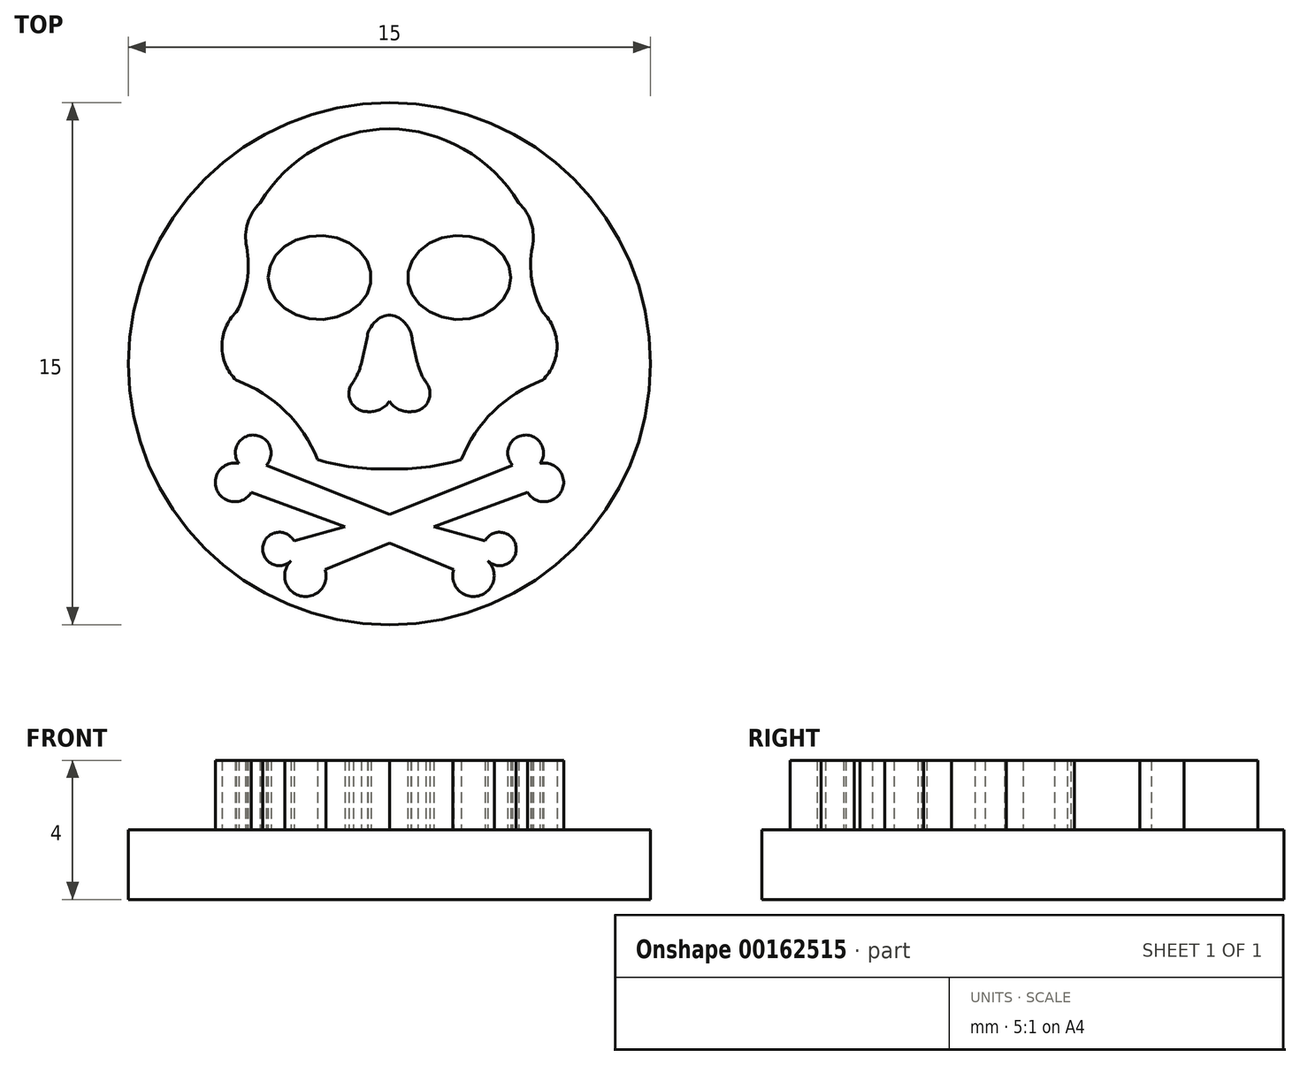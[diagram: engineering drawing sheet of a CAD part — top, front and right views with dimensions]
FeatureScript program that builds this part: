
annotation { "Feature Type Name" : "Feature", "Feature Type Description" : "" }
export const myFeature = defineFeature(function(context is Context, id is Id, definition is map)
    precondition{}
    {
        {
            var Q0;
            Q0=qCreatedBy(makeId("Top.planeOp"),FACE);
            var sketch = newSketch(context, id + "F0", { "sketchPlane" : qUnion([Q0])});
            skCircle(sketch, "E0", {"center": v(0, 0) * mm, "radius": 7.5 * mm});
            skSolve(sketch);
        }
        {
            var Q0;
            Q0=makeQuery(id+"F0.imprint","IMPRINT",FACE,{"disambiguationData":[TD([[makeQuery(id+"F0.imprint","IMPRINT",EDGE,{"derivedFrom":sQuery(id+"F0.wireOp",EDGE,"E0")}),1.0]])]});
            extrude(context, id + "F1", {"entities" : qUnion([Q0]), "depth" : 2 * mm});
        }
        {
            var Q0;
            Q0=makeQuery(id+"F1.opExtrude","CAP_FACE",FACE,{"disambiguationData":[OSD([sQuery(id+"F0.wireOp",EDGE,"E0")])],"isStart":false});
            var sketch = newSketch(context, id + "F2", { "sketchPlane" : qUnion([Q0])});
            skLineSegment(sketch, "E1", {"start": v(0, 8.52) * mm, "end": v(0, -8.58) * mm, "construction": true});
            skArc(sketch, "E2", {"start": v(-3.71, 4.63) * mm, "mid": v(-4.07, 4.04) * mm, "end": v(-4.1, 3.36) * mm});
            skArc(sketch, "E3", {"start": v(-4.4, 1.48) * mm, "mid": v(-4.1, 2.4) * mm, "end": v(-4.1, 3.36) * mm});
            skArc(sketch, "E4", {"start": v(-4.4, 1.48) * mm, "mid": v(-4.81, 0.5) * mm, "end": v(-4.4, -0.48) * mm});
            skArc(sketch, "E5", {"start": v(-2.06, -2.76) * mm, "mid": v(-2.99, -1.37) * mm, "end": v(-4.4, -0.48) * mm});
            skArc(sketch, "E6.trimOffspring", {"start": v(-3.71, 4.63) * mm, "mid": v(-3.72, 4.62) * mm, "end": v(-3.73, 4.6) * mm});
            skArc(sketch, "E7", {"start": v(0, 6.75) * mm, "mid": v(-2.13, 6.17) * mm, "end": v(-3.71, 4.63) * mm});
            skPoint(sketch, "E8.midSnap0", {"position": v(0, -1.4) * mm});
            skPoint(sketch, "E8.midSnap1", {"position": v(-0.81, 0) * mm});
            skEllipticalArc(sketch, "E9.trimOffspring", {});
            skPoint(sketch, "E8.end.orphan", {"position": v(0, -1.4) * mm});
            skPoint(sketch, "E8.start.orphan", {"position": v(-0.81, 0) * mm});
            skArc(sketch, "E10", {"start": v(-1.04, -0.52) * mm, "mid": v(-0.9, -0.27) * mm, "end": v(-0.81, 0) * mm});
            skArc(sketch, "E11", {"start": v(-1.04, -0.52) * mm, "mid": v(-1.11, -1.08) * mm, "end": v(-0.63, -1.38) * mm});
            skArc(sketch, "E12", {"start": v(-0.63, -1.38) * mm, "mid": v(-0.28, -1.32) * mm, "end": v(0, -1.08) * mm});
            skPoint(sketch, "E12.endSnap0", {"position": v(-1.11, -1.08) * mm});
            skPoint(sketch, "E13.end.orphan", {"position": v(-0.81, -0.48) * mm});
            skArc(sketch, "E14", {"start": v(-0.81, 0) * mm, "mid": v(-0.7, 0.45) * mm, "end": v(-0.62, 0.9) * mm});
            skEllipse(sketch, "E15", {"center": v(-2, 2.48) * mm, "majorRadius": 1.48 * mm, "minorRadius": 1.2 * mm, "majorAxis": v(-1, 0)});
            skArc(sketch, "E16", {"start": v(-2.06, -2.76) * mm, "mid": v(-1.04, -2.97) * mm, "end": v(0, -3.02) * mm});
            skLineSegment(sketch, "E17", {"start": v(0, 7.86) * mm, "end": v(0, -9.52) * mm, "construction": true});
            skArc(sketch, "E18.MirrorCS", {"start": v(0, 6.75) * mm, "mid": v(2.13, 6.17) * mm, "end": v(3.71, 4.63) * mm});
            skArc(sketch, "E19.MirrorCS", {"start": v(3.71, 4.63) * mm, "mid": v(4.07, 4.04) * mm, "end": v(4.1, 3.36) * mm});
            skArc(sketch, "E20.MirrorCS", {"start": v(4.4, 1.48) * mm, "mid": v(4.1, 2.4) * mm, "end": v(4.1, 3.36) * mm});
            skArc(sketch, "E21.MirrorCS", {"start": v(4.4, 1.48) * mm, "mid": v(4.81, 0.5) * mm, "end": v(4.4, -0.48) * mm});
            skArc(sketch, "E22.MirrorCS", {"start": v(2.06, -2.76) * mm, "mid": v(2.99, -1.37) * mm, "end": v(4.4, -0.48) * mm});
            skArc(sketch, "E23.MirrorCS", {"start": v(2.06, -2.76) * mm, "mid": v(1.04, -2.97) * mm, "end": v(0, -3.02) * mm});
            skEllipse(sketch, "E24.MirrorC", {"center": v(2, 2.48) * mm, "majorRadius": 1.48 * mm, "minorRadius": 1.2 * mm, "majorAxis": v(1, 0)});
            skEllipticalArc(sketch, "E25.MirrorCS", {});
            skArc(sketch, "E26.MirrorCS", {"start": v(0.81, 0) * mm, "mid": v(0.7, 0.45) * mm, "end": v(0.62, 0.9) * mm});
            skArc(sketch, "E27.MirrorCS", {"start": v(1.04, -0.52) * mm, "mid": v(0.9, -0.27) * mm, "end": v(0.81, 0) * mm});
            skArc(sketch, "E28.MirrorCS", {"start": v(1.04, -0.52) * mm, "mid": v(1.11, -1.08) * mm, "end": v(0.63, -1.38) * mm});
            skArc(sketch, "E29.MirrorCS", {"start": v(0.63, -1.38) * mm, "mid": v(0.28, -1.32) * mm, "end": v(0, -1.08) * mm});
            const initialGuessF2  = {"E9.trimOffspring": [0, 0, -1, 0, 0.0008127465844154358, 0.0013945407185848731, 4.71238898038469, 5.57540933718284], "E25.MirrorCS": [0, 0, 1, 0, 0.0008127465844154358, 0.0013945407185848731, 0.7077759699967459, 1.5707963267948966]};
            skSetInitialGuess(sketch, initialGuessF2);
            skSolve(sketch);
        }
        {
            var Q0;
            Q0 = qSketchRegion(id + "F2", true);
            extrude(context, id + "F3", {"entities" : qUnion([Q0]), "operationType" : NewBodyOperationType.ADD, "depth" : 2 * mm});
        }
        {
            var Q0;
            {var subQ0=sQuery(id+"F0.wireOp",EDGE,"E0");Q0=makeQuery(id+"F3.boolean.opBoolean","SPLIT",FACE,{"disambiguationData":[TD([makeQuery(id+"F1.opExtrude","SWEPT_FACE",FACE,{"disambiguationData":[OSD([subQ0])]})])],"derivedFrom":makeQuery(id+"F1.opExtrude","CAP_FACE",FACE,{"disambiguationData":[OSD([subQ0])],"isStart":false})});}
            var sketch = newSketch(context, id + "F4", { "sketchPlane" : qUnion([Q0])});
            skPoint(sketch, "E30.trimOffspring.end.orphan", {"position": v(0, 0) * mm});
            skPoint(sketch, "E31.start.orphan", {"position": v(0, -9.94) * mm});
            skLineSegment(sketch, "E32", {"start": v(0, 0) * mm, "end": v(0, -8.01) * mm, "construction": true});
            skArc(sketch, "E33", {"start": v(-3.54, -2.92) * mm, "mid": v(-3.88, -2.05) * mm, "end": v(-4.33, -2.87) * mm});
            skArc(sketch, "E34", {"start": v(-4.33, -2.87) * mm, "mid": v(-4.96, -3.63) * mm, "end": v(-3.97, -3.7) * mm});
            skArc(sketch, "E35", {"start": v(-2.74, -5.1) * mm, "mid": v(-3.64, -5.25) * mm, "end": v(-2.83, -5.67) * mm});
            skArc(sketch, "E36", {"start": v(-2.83, -5.67) * mm, "mid": v(-2.56, -6.67) * mm, "end": v(-1.85, -5.92) * mm});
            skLineSegment(sketch, "E37", {"start": v(-3.54, -2.92) * mm, "end": v(0, -4.33) * mm});
            skLineSegment(sketch, "E38", {"start": v(-3.97, -3.7) * mm, "end": v(-1.28, -4.69) * mm});
            skLineSegment(sketch, "E39", {"start": v(-2.74, -5.1) * mm, "end": v(-1.28, -4.69) * mm});
            skLineSegment(sketch, "E40", {"start": v(-1.85, -5.92) * mm, "end": v(0, -5.15) * mm});
            skArc(sketch, "E41.MirrorC", {"start": v(3.54, -2.92) * mm, "mid": v(3.88, -2.05) * mm, "end": v(4.33, -2.87) * mm});
            skArc(sketch, "E42.MirrorC", {"start": v(4.33, -2.87) * mm, "mid": v(4.96, -3.63) * mm, "end": v(3.97, -3.7) * mm});
            skLineSegment(sketch, "E43.MirrorCS", {"start": v(3.54, -2.92) * mm, "end": v(0, -4.33) * mm});
            skLineSegment(sketch, "E44.MirrorCS", {"start": v(3.97, -3.7) * mm, "end": v(1.28, -4.69) * mm});
            skLineSegment(sketch, "E45.MirrorCS", {"start": v(2.74, -5.1) * mm, "end": v(1.28, -4.69) * mm});
            skLineSegment(sketch, "E46.MirrorCS", {"start": v(1.85, -5.92) * mm, "end": v(0, -5.15) * mm});
            skArc(sketch, "E47.MirrorC", {"start": v(2.74, -5.1) * mm, "mid": v(3.64, -5.25) * mm, "end": v(2.83, -5.67) * mm});
            skArc(sketch, "E48.MirrorC", {"start": v(2.83, -5.67) * mm, "mid": v(2.56, -6.67) * mm, "end": v(1.85, -5.92) * mm});
            skPoint(sketch, "E49.orphan", {"position": v(0, -4.33) * mm});
            skPoint(sketch, "E50.orphan", {"position": v(0, -5.15) * mm});
            skSolve(sketch);
        }
        {
            var Q0;
            Q0 = qSketchRegion(id + "F4", true);
            extrude(context, id + "F5", {"entities" : qUnion([Q0]), "operationType" : NewBodyOperationType.ADD, "depth" : 2 * mm});
        }
    });
